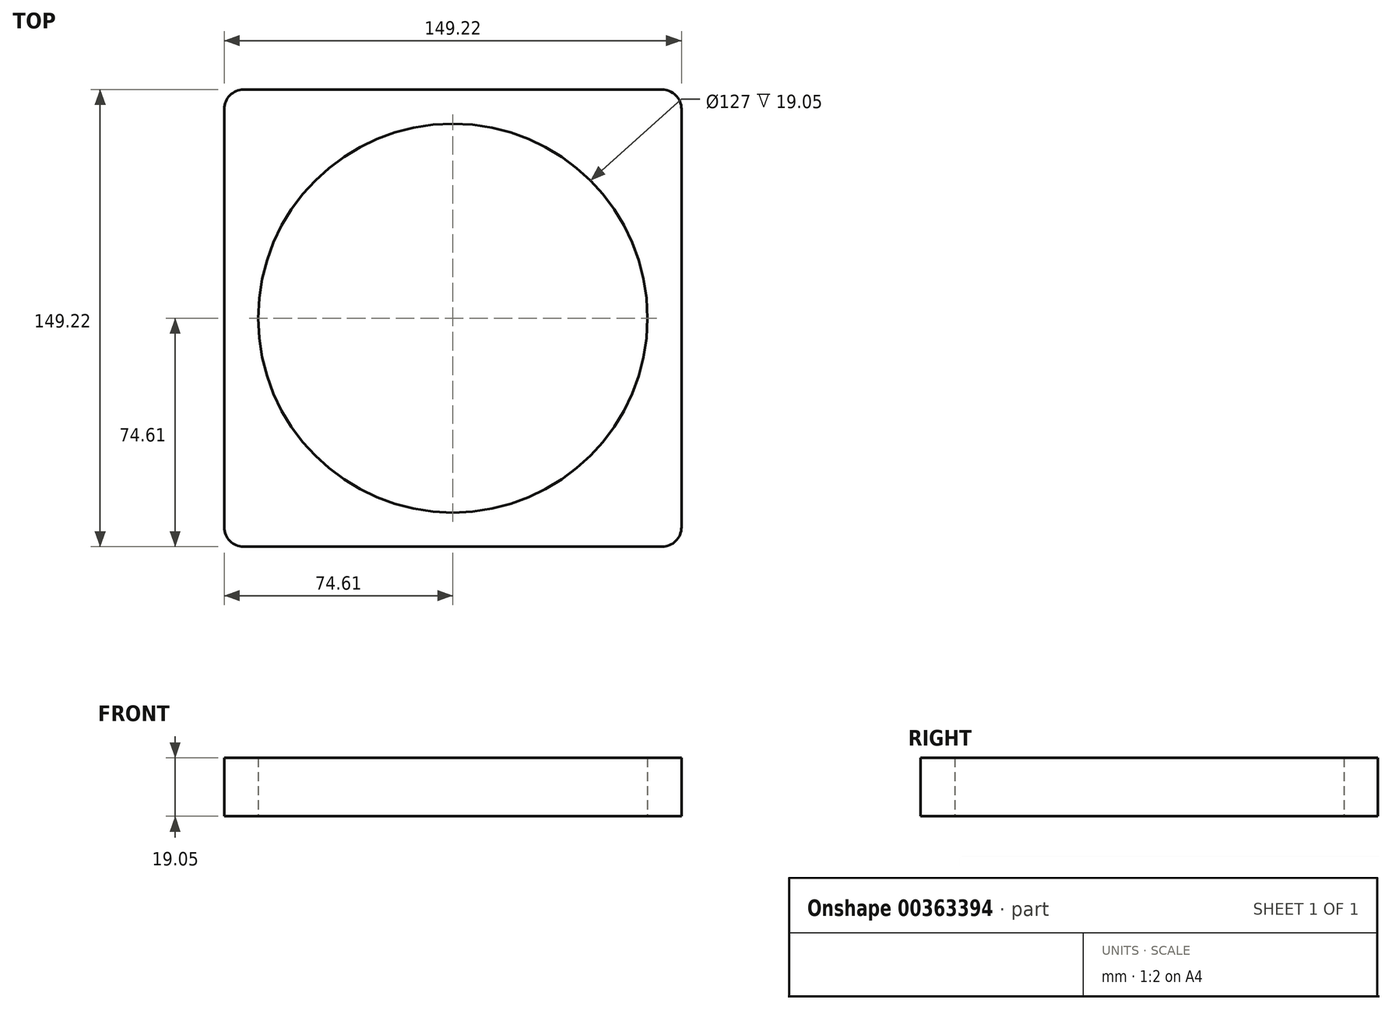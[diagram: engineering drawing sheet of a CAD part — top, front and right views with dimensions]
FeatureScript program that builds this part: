
annotation { "Feature Type Name" : "Feature", "Feature Type Description" : "" }
export const myFeature = defineFeature(function(context is Context, id is Id, definition is map)
    precondition{}
    {
        {
            var Q0;
            Q0=qCreatedBy(makeId("Top.planeOp"),FACE);
            var sketch = newSketch(context, id + "F0", { "sketchPlane" : qUnion([Q0])});
            skLineSegment(sketch, "E0.bottom", {"start": v(-68.26, 74.61) * mm, "end": v(68.26, 74.61) * mm});
            skLineSegment(sketch, "E0.top", {"start": v(-68.26, -74.61) * mm, "end": v(68.26, -74.61) * mm});
            skLineSegment(sketch, "E0.left", {"start": v(-74.61, 68.26) * mm, "end": v(-74.61, -68.26) * mm});
            skLineSegment(sketch, "E0.right", {"start": v(74.61, 68.26) * mm, "end": v(74.61, -68.26) * mm});
            skPoint(sketch, "E0.middle", {"position": v(0, 0) * mm});
            skCircle(sketch, "E1", {"center": v(0, 0) * mm, "radius": 63.5 * mm});
            skPoint(sketch, "E2.visualSharp", {"position": v(-74.61, 74.61) * mm});
            skArc(sketch, "E2.filletArc", {"start": v(-68.26, 74.61) * mm, "mid": v(-72.75, 72.75) * mm, "end": v(-74.61, 68.26) * mm});
            skPoint(sketch, "E3.visualSharp", {"position": v(74.61, 74.61) * mm});
            skArc(sketch, "E3.filletArc", {"start": v(74.61, 68.26) * mm, "mid": v(72.75, 72.75) * mm, "end": v(68.26, 74.61) * mm});
            skPoint(sketch, "E4.visualSharp", {"position": v(74.61, -74.61) * mm});
            skArc(sketch, "E4.filletArc", {"start": v(68.26, -74.61) * mm, "mid": v(72.75, -72.75) * mm, "end": v(74.61, -68.26) * mm});
            skPoint(sketch, "E5.visualSharp", {"position": v(-74.61, -74.61) * mm});
            skArc(sketch, "E5.filletArc", {"start": v(-74.61, -68.26) * mm, "mid": v(-72.75, -72.75) * mm, "end": v(-68.26, -74.61) * mm});
            skSolve(sketch);
        }
        {
            var Q0;
            Q0=makeQuery(id+"F0.imprint","IMPRINT",FACE,{"disambiguationData":[TD([[makeQuery(id+"F0.imprint","IMPRINT",EDGE,{"derivedFrom":sQuery(id+"F0.wireOp",EDGE,"E0.bottom")}),-1.0]])]});
            extrude(context, id + "F1", {"entities" : qUnion([Q0]), "depth" : 19.05 * mm});
        }
    });
